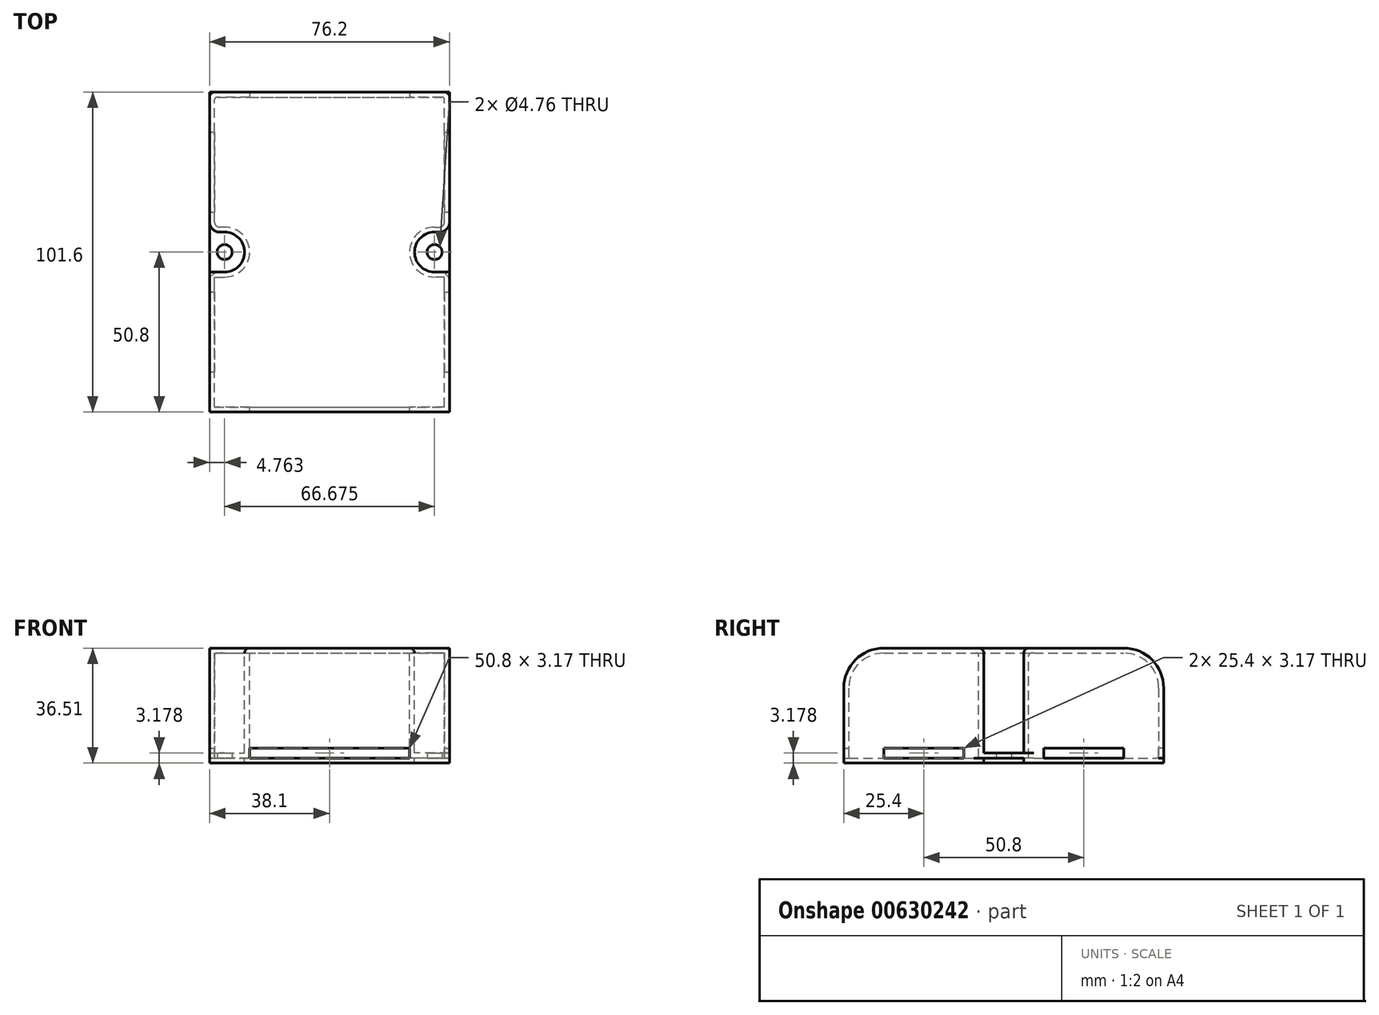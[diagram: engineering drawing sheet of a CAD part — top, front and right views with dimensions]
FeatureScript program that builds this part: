
annotation { "Feature Type Name" : "Feature", "Feature Type Description" : "" }
export const myFeature = defineFeature(function(context is Context, id is Id, definition is map)
    precondition{}
    {
        {
            var Q0;
            Q0=qCreatedBy(makeId("Top.planeOp"),FACE);
            var sketch = newSketch(context, id + "F0", { "sketchPlane" : qUnion([Q0])});
            skLineSegment(sketch, "E0.bottom", {"start": v(38.1, -50.8) * mm, "end": v(-38.1, -50.8) * mm});
            skLineSegment(sketch, "E0.top", {"start": v(38.1, 50.8) * mm, "end": v(-38.1, 50.8) * mm});
            skLineSegment(sketch, "E0.left", {"start": v(38.1, -50.8) * mm, "end": v(38.1, 50.8) * mm});
            skLineSegment(sketch, "E0.right", {"start": v(-38.1, -50.8) * mm, "end": v(-38.1, 50.8) * mm});
            skPoint(sketch, "E0.middle", {"position": v(0, 0) * mm});
            skSolve(sketch);
        }
        {
            var Q0;
            Q0 = qSketchRegion(id + "F0", true);
            extrude(context, id + "F1", {"entities" : qUnion([Q0]), "oppositeDirection" : true, "depth" : 1.59 * mm, "offsetDistance" : 25.4 * mm});
        }
        {
            var Q0;
            Q0=makeQuery(id+"F1.opExtrude","CAP_FACE",FACE,{"disambiguationData":[OSD([sQuery(id+"F0.wireOp",EDGE,"E0.bottom"),sQuery(id+"F0.wireOp",EDGE,"E0.top"),sQuery(id+"F0.wireOp",EDGE,"E0.left"),sQuery(id+"F0.wireOp",EDGE,"E0.right")])],"isStart":true});
            var sketch = newSketch(context, id + "F2", { "sketchPlane" : qUnion([Q0])});
            skLineSegment(sketch, "E1", {"start": v(0, 0) * mm, "end": v(57.42, 0) * mm, "construction": true});
            skLineSegment(sketch, "E2", {"start": v(0, 0) * mm, "end": v(0, 58.88) * mm, "construction": true});
            skPoint(sketch, "E2.endSnap0", {"position": v(0, 50.8) * mm});
            skLineSegment(sketch, "E3", {"start": v(0, 0) * mm, "end": v(-42.8, 0) * mm, "construction": true});
            skCircle(sketch, "E4", {"center": v(33.34, 0) * mm, "radius": 2.38 * mm});
            skCircle(sketch, "E5", {"center": v(-33.34, 0) * mm, "radius": 2.38 * mm});
            skSolve(sketch);
        }
        {
            var Q0;
            Q0 = qSketchRegion(id + "F2", true);
            extrude(context, id + "F3", {"entities" : qUnion([Q0]), "operationType" : NewBodyOperationType.REMOVE, "endBound" : BoundingType.THROUGH_ALL, "oppositeDirection" : true, "depth" : 25.4 * mm, "offsetDistance" : 25.4 * mm});
        }
        {
            var Q0;
            Q0=makeQuery(id+"F1.opExtrude","CAP_FACE",FACE,{"disambiguationData":[OSD([sQuery(id+"F0.wireOp",EDGE,"E0.bottom"),sQuery(id+"F0.wireOp",EDGE,"E0.top"),sQuery(id+"F0.wireOp",EDGE,"E0.left"),sQuery(id+"F0.wireOp",EDGE,"E0.right")])],"isStart":true});
            var sketch = newSketch(context, id + "F4", { "sketchPlane" : qUnion([Q0])});
            skLineSegment(sketch, "E6.0", {"start": v(38.1, 50.8) * mm, "end": v(-38.1, 50.8) * mm});
            skLineSegment(sketch, "E6.1", {"start": v(38.1, -50.8) * mm, "end": v(38.1, 50.8) * mm});
            skLineSegment(sketch, "E6.2", {"start": v(38.1, -50.8) * mm, "end": v(-38.1, -50.8) * mm});
            skLineSegment(sketch, "E6.3", {"start": v(-38.1, -50.8) * mm, "end": v(-38.1, 50.8) * mm});
            skSolve(sketch);
        }
        {
            var Q0;
            Q0 = qSketchRegion(id + "F4", true);
            extrude(context, id + "F5", {"entities" : qUnion([Q0]), "depth" : 34.92 * mm, "offsetDistance" : 25.4 * mm});
        }
        {
            var Q0;
            Q0=makeQuery(id+"F5.opExtrude","CAP_EDGE",EDGE,{"disambiguationData":[OSD([sQuery(id+"F4.wireOp",EDGE,"E6.2")])],"isStart":false});
            var Q1;
            Q1=makeQuery(id+"F5.opExtrude","CAP_EDGE",EDGE,{"disambiguationData":[OSD([sQuery(id+"F4.wireOp",EDGE,"E6.0")])],"isStart":false});
            fillet(context, id + "F6", {"entities" : qUnion([Q0, Q1]), "radius" : 12.7 * mm, "tangentPropagation" : true, "allowEdgeOverflow" : false});
        }
        {
            var Q0;
            Q0=makeQuery(id+"F5.opExtrude","CAP_FACE",FACE,{"disambiguationData":[OSD([sQuery(id+"F4.wireOp",EDGE,"E6.0"),sQuery(id+"F4.wireOp",EDGE,"E6.1"),sQuery(id+"F4.wireOp",EDGE,"E6.2"),sQuery(id+"F4.wireOp",EDGE,"E6.3")])],"isStart":false});
            var sketch = newSketch(context, id + "F7", { "sketchPlane" : qUnion([Q0])});
            skLineSegment(sketch, "E7", {"start": v(-38.1, 6.35) * mm, "end": v(-38.1, -6.35) * mm});
            skLineSegment(sketch, "E8", {"start": v(-38.1, -6.35) * mm, "end": v(-33.34, -6.35) * mm});
            skArc(sketch, "E9", {"start": v(-33.34, -6.35) * mm, "mid": v(-26.99, 0) * mm, "end": v(-33.34, 6.35) * mm});
            skLineSegment(sketch, "E10", {"start": v(-33.34, 6.35) * mm, "end": v(-38.1, 6.35) * mm});
            skPoint(sketch, "E11", {"position": v(-26.99, 0) * mm});
            skLineSegment(sketch, "E12", {"start": v(0, 0) * mm, "end": v(0, -55.43) * mm, "construction": true});
            skPoint(sketch, "E13.MirrorP", {"position": v(26.99, 0) * mm});
            skLineSegment(sketch, "E14.MirrorCS", {"start": v(38.1, 6.35) * mm, "end": v(38.1, -6.35) * mm});
            skLineSegment(sketch, "E15.MirrorCS", {"start": v(38.1, -6.35) * mm, "end": v(33.34, -6.35) * mm});
            skLineSegment(sketch, "E16.MirrorCS", {"start": v(33.34, 6.35) * mm, "end": v(38.1, 6.35) * mm});
            skArc(sketch, "E17.MirrorCS", {"start": v(33.34, -6.35) * mm, "mid": v(26.99, 0) * mm, "end": v(33.34, 6.35) * mm});
            skSolve(sketch);
        }
        {
            var Q0;
            Q0 = qSketchRegion(id + "F7", true);
            extrude(context, id + "F8", {"entities" : qUnion([Q0]), "operationType" : NewBodyOperationType.REMOVE, "endBound" : BoundingType.THROUGH_ALL, "oppositeDirection" : true, "depth" : 25.4 * mm, "offsetDistance" : 25.4 * mm});
        }
        {
            var Q0;
            Q0=makeQuery(id+"F8.boolean.opBoolean","COPY",EDGE,{"derivedFrom":makeQuery(id+"F8.opExtrude","SWEPT_EDGE",EDGE,{"disambiguationData":[OSD([sQuery(id+"F4.wireOp",EDGE,"E6.1"),sQuery(id+"F7.wireOp",EDGE,"E14.MirrorCS"),sQuery(id+"F7.wireOp",EDGE,"E15.MirrorCS")])]})});
            var Q1;
            Q1=makeQuery(id+"F8.boolean.opBoolean","COPY",EDGE,{"derivedFrom":makeQuery(id+"F8.opExtrude","SWEPT_EDGE",EDGE,{"disambiguationData":[OSD([sQuery(id+"F4.wireOp",EDGE,"E6.1"),sQuery(id+"F7.wireOp",EDGE,"E14.MirrorCS"),sQuery(id+"F7.wireOp",EDGE,"E16.MirrorCS")])]})});
            var Q2;
            Q2=makeQuery(id+"F8.boolean.opBoolean","COPY",EDGE,{"derivedFrom":makeQuery(id+"F8.opExtrude","SWEPT_EDGE",EDGE,{"disambiguationData":[OSD([sQuery(id+"F4.wireOp",EDGE,"E6.3"),sQuery(id+"F7.wireOp",EDGE,"E7"),sQuery(id+"F7.wireOp",EDGE,"E8")])]})});
            var Q3;
            Q3=makeQuery(id+"F8.boolean.opBoolean","COPY",EDGE,{"derivedFrom":makeQuery(id+"F8.opExtrude","SWEPT_EDGE",EDGE,{"disambiguationData":[OSD([sQuery(id+"F4.wireOp",EDGE,"E6.3"),sQuery(id+"F7.wireOp",EDGE,"E7"),sQuery(id+"F7.wireOp",EDGE,"E10")])]})});
            fillet(context, id + "F9", {"entities" : qUnion([Q0, Q1, Q2, Q3]), "radius" : 3.17 * mm, "tangentPropagation" : true, "allowEdgeOverflow" : false});
        }
        {
            var Q0;
            Q0=makeQuery(id+"F5.opExtrude","CAP_FACE",FACE,{"disambiguationData":[OSD([sQuery(id+"F4.wireOp",EDGE,"E6.0"),sQuery(id+"F4.wireOp",EDGE,"E6.1"),sQuery(id+"F4.wireOp",EDGE,"E6.2"),sQuery(id+"F4.wireOp",EDGE,"E6.3")])],"isStart":true});
            shell(context, id + "F10", {"entities" : qUnion([Q0]), "thickness" : 1.59 * mm});
        }
        {
            var Q0;
            Q0=makeQuery(id+"F5.opExtrude","SWEPT_EDGE",EDGE,{"disambiguationData":[OSD([sQuery(id+"F4.wireOp",EDGE,"E6.0"),sQuery(id+"F4.wireOp",EDGE,"E6.3")])]});
            var Q1;
            Q1=makeQuery(id+"F5.opExtrude","SWEPT_EDGE",EDGE,{"disambiguationData":[OSD([sQuery(id+"F4.wireOp",EDGE,"E6.0"),sQuery(id+"F4.wireOp",EDGE,"E6.1")])]});
            fillet(context, id + "F11", {"entities" : qUnion([Q0, Q1]), "radius" : 1.59 * mm, "tangentPropagation" : true, "allowEdgeOverflow" : false});
        }
        {
            var Q0;
            {var subQ0=sQuery(id+"F4.wireOp",EDGE,"E6.3");var subQ1=sQuery(id+"F4.wireOp",EDGE,"E6.0");Q0=makeQuery(id+"F10.opShell","OFFSET_EDGE",EDGE,{"disambiguationData":[OSD([subQ1,subQ0]),TDD([makeQuery(id+"F5.opExtrude","SWEPT_EDGE",EDGE,{"disambiguationData":[OSD([subQ1,subQ0])]})])]});}
            var Q1;
            {var subQ0=sQuery(id+"F4.wireOp",EDGE,"E6.1");var subQ1=sQuery(id+"F4.wireOp",EDGE,"E6.0");Q1=makeQuery(id+"F10.opShell","OFFSET_EDGE",EDGE,{"disambiguationData":[OSD([subQ1,subQ0]),TDD([makeQuery(id+"F5.opExtrude","SWEPT_EDGE",EDGE,{"disambiguationData":[OSD([subQ1,subQ0])]})])]});}
            fillet(context, id + "F12", {"entities" : qUnion([Q0, Q1]), "radius" : 0.8 * mm, "tangentPropagation" : true, "allowEdgeOverflow" : false});
        }
        {
            var Q0;
            Q0=makeQuery(id+"F5.opExtrude","CAP_FACE",FACE,{"disambiguationData":[OSD([sQuery(id+"F4.wireOp",EDGE,"E6.0"),sQuery(id+"F4.wireOp",EDGE,"E6.1"),sQuery(id+"F4.wireOp",EDGE,"E6.2"),sQuery(id+"F4.wireOp",EDGE,"E6.3")])],"isStart":true});
            var sketch = newSketch(context, id + "F13", { "sketchPlane" : qUnion([Q0])});
            skArc(sketch, "E18.0", {"start": v(-38.1, 9.53) * mm, "mid": v(-37.17, 7.28) * mm, "end": v(-34.92, 6.35) * mm});
            skLineSegment(sketch, "E18.1", {"start": v(-34.92, 6.35) * mm, "end": v(-33.34, 6.35) * mm});
            skArc(sketch, "E18.2", {"start": v(-33.34, 6.35) * mm, "mid": v(-26.99, 0) * mm, "end": v(-33.34, -6.35) * mm});
            skLineSegment(sketch, "E18.3", {"start": v(-33.34, -6.35) * mm, "end": v(-34.92, -6.35) * mm});
            skArc(sketch, "E18.4", {"start": v(-34.92, -6.35) * mm, "mid": v(-37.17, -7.28) * mm, "end": v(-38.1, -9.53) * mm});
            skLineSegment(sketch, "E19", {"start": v(-38.1, 9.53) * mm, "end": v(-38.1, -9.53) * mm});
            skArc(sketch, "E20.0", {"start": v(34.93, 6.35) * mm, "mid": v(37.17, 7.28) * mm, "end": v(38.1, 9.53) * mm});
            skLineSegment(sketch, "E20.1", {"start": v(34.93, 6.35) * mm, "end": v(33.34, 6.35) * mm});
            skArc(sketch, "E20.2", {"start": v(33.34, 6.35) * mm, "mid": v(26.99, 0) * mm, "end": v(33.34, -6.35) * mm});
            skLineSegment(sketch, "E20.3", {"start": v(33.34, -6.35) * mm, "end": v(34.93, -6.35) * mm});
            skArc(sketch, "E20.4", {"start": v(38.1, -9.53) * mm, "mid": v(37.17, -7.28) * mm, "end": v(34.93, -6.35) * mm});
            skLineSegment(sketch, "E21", {"start": v(38.1, 9.53) * mm, "end": v(38.1, -9.53) * mm});
            skSolve(sketch);
        }
        {
            var Q0;
            Q0 = qSketchRegion(id + "F13", true);
            extrude(context, id + "F14", {"entities" : qUnion([Q0]), "operationType" : NewBodyOperationType.ADD, "oppositeDirection" : true, "depth" : 1.59 * mm, "offsetDistance" : 25.4 * mm});
        }
        {
            var Q0;
            Q0=makeQuery(id+"F14.boolean.opBoolean","MERGE",FACE,{"derivedFrom":[makeQuery(id+"F5.opExtrude","CAP_FACE",FACE,{"disambiguationData":[OSD([sQuery(id+"F4.wireOp",EDGE,"E6.0"),sQuery(id+"F4.wireOp",EDGE,"E6.1"),sQuery(id+"F4.wireOp",EDGE,"E6.2"),sQuery(id+"F4.wireOp",EDGE,"E6.3")])],"isStart":true}),makeQuery(id+"F14.opExtrude","CAP_FACE",FACE,{"disambiguationData":[OSD([sQuery(id+"F13.wireOp",EDGE,"E18.0"),sQuery(id+"F13.wireOp",EDGE,"E18.1"),sQuery(id+"F13.wireOp",EDGE,"E18.2"),sQuery(id+"F13.wireOp",EDGE,"E18.3"),sQuery(id+"F13.wireOp",EDGE,"E18.4"),sQuery(id+"F13.wireOp",EDGE,"E19")])],"isStart":true}),makeQuery(id+"F14.opExtrude","CAP_FACE",FACE,{"disambiguationData":[OSD([sQuery(id+"F13.wireOp",EDGE,"E20.0"),sQuery(id+"F13.wireOp",EDGE,"E20.1"),sQuery(id+"F13.wireOp",EDGE,"E20.2"),sQuery(id+"F13.wireOp",EDGE,"E20.3"),sQuery(id+"F13.wireOp",EDGE,"E20.4"),sQuery(id+"F13.wireOp",EDGE,"E21")])],"isStart":true})]});
            var sketch = newSketch(context, id + "F15", { "sketchPlane" : qUnion([Q0])});
            skCircle(sketch, "E22.0", {"center": v(-33.34, 0) * mm, "radius": 2.38 * mm});
            skCircle(sketch, "E22.1", {"center": v(33.34, 0) * mm, "radius": 2.38 * mm});
            skSolve(sketch);
        }
        {
            var Q0;
            Q0 = qSketchRegion(id + "F15", true);
            extrude(context, id + "F16", {"entities" : qUnion([Q0]), "operationType" : NewBodyOperationType.REMOVE, "oppositeDirection" : true, "depth" : 25.4 * mm, "offsetDistance" : 25.4 * mm});
        }
        {
            var Q0;
            Q0=makeQuery(id+"F14.boolean.opBoolean","MERGE",FACE,{"derivedFrom":[makeQuery(id+"F5.opExtrude","CAP_FACE",FACE,{"disambiguationData":[OSD([sQuery(id+"F4.wireOp",EDGE,"E6.0"),sQuery(id+"F4.wireOp",EDGE,"E6.1"),sQuery(id+"F4.wireOp",EDGE,"E6.2"),sQuery(id+"F4.wireOp",EDGE,"E6.3")])],"isStart":true}),makeQuery(id+"F14.opExtrude","CAP_FACE",FACE,{"disambiguationData":[OSD([sQuery(id+"F13.wireOp",EDGE,"E18.0"),sQuery(id+"F13.wireOp",EDGE,"E18.1"),sQuery(id+"F13.wireOp",EDGE,"E18.2"),sQuery(id+"F13.wireOp",EDGE,"E18.3"),sQuery(id+"F13.wireOp",EDGE,"E18.4"),sQuery(id+"F13.wireOp",EDGE,"E19")])],"isStart":true}),makeQuery(id+"F14.opExtrude","CAP_FACE",FACE,{"disambiguationData":[OSD([sQuery(id+"F13.wireOp",EDGE,"E20.0"),sQuery(id+"F13.wireOp",EDGE,"E20.1"),sQuery(id+"F13.wireOp",EDGE,"E20.2"),sQuery(id+"F13.wireOp",EDGE,"E20.3"),sQuery(id+"F13.wireOp",EDGE,"E20.4"),sQuery(id+"F13.wireOp",EDGE,"E21")])],"isStart":true})]});
            var sketch = newSketch(context, id + "F17", { "sketchPlane" : qUnion([Q0])});
            skLineSegment(sketch, "E23.bottom", {"start": v(-25.4, 63.5) * mm, "end": v(25.4, 63.5) * mm});
            skLineSegment(sketch, "E23.left", {"start": v(-25.4, 63.5) * mm, "end": v(-25.4, 38.1) * mm});
            skLineSegment(sketch, "E23.right", {"start": v(25.4, 63.5) * mm, "end": v(25.4, 38.1) * mm});
            skLineSegment(sketch, "E24.bottom", {"start": v(-50.8, 12.7) * mm, "end": v(50.8, 12.7) * mm});
            skLineSegment(sketch, "E24.top", {"start": v(-50.8, 38.1) * mm, "end": v(-25.4, 38.1) * mm});
            skLineSegment(sketch, "E24.left", {"start": v(-50.8, 12.7) * mm, "end": v(-50.8, 38.1) * mm});
            skLineSegment(sketch, "E24.right", {"start": v(50.8, 12.7) * mm, "end": v(50.8, 38.1) * mm});
            skLineSegment(sketch, "E25", {"start": v(0, 0) * mm, "end": v(0, 63.44) * mm, "construction": true});
            skLineSegment(sketch, "E26", {"start": v(0, 0) * mm, "end": v(64.68, 0) * mm, "construction": true});
            skPoint(sketch, "E26.endSnap0", {"position": v(25.4, 0) * mm});
            skLineSegment(sketch, "E27.trimOffspring", {"start": v(25.4, 38.1) * mm, "end": v(50.8, 38.1) * mm});
            skLineSegment(sketch, "E28.MirrorCS", {"start": v(25.4, -38.1) * mm, "end": v(50.8, -38.1) * mm});
            skLineSegment(sketch, "E29.MirrorCS", {"start": v(-25.4, -63.5) * mm, "end": v(25.4, -63.5) * mm});
            skLineSegment(sketch, "E30.MirrorCS", {"start": v(-25.4, -63.5) * mm, "end": v(-25.4, -38.1) * mm});
            skLineSegment(sketch, "E31.MirrorCS", {"start": v(25.4, -63.5) * mm, "end": v(25.4, -38.1) * mm});
            skLineSegment(sketch, "E32.MirrorCS", {"start": v(-50.8, -12.7) * mm, "end": v(50.8, -12.7) * mm});
            skLineSegment(sketch, "E33.MirrorCS", {"start": v(-50.8, -38.1) * mm, "end": v(-25.4, -38.1) * mm});
            skLineSegment(sketch, "E34.MirrorCS", {"start": v(-50.8, -12.7) * mm, "end": v(-50.8, -38.1) * mm});
            skLineSegment(sketch, "E35.MirrorCS", {"start": v(50.8, -12.7) * mm, "end": v(50.8, -38.1) * mm});
            skSolve(sketch);
        }
        {
            var Q0;
            Q0 = qSketchRegion(id + "F17", true);
            extrude(context, id + "F18", {"entities" : qUnion([Q0]), "operationType" : NewBodyOperationType.REMOVE, "oppositeDirection" : true, "depth" : 3.17 * mm, "offsetDistance" : 25.4 * mm});
        }
    });
